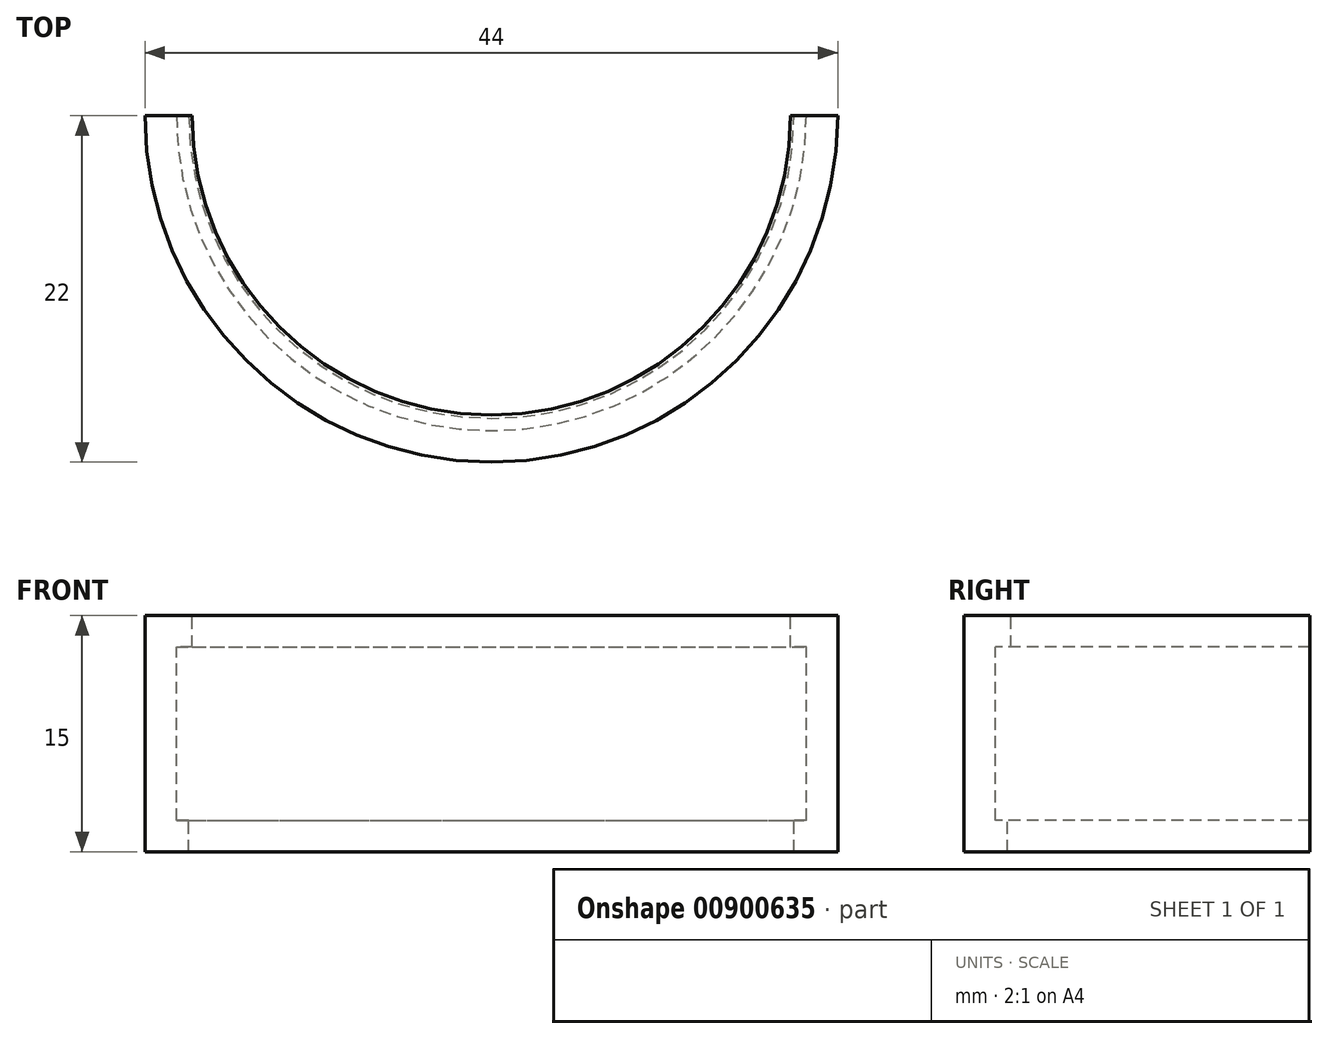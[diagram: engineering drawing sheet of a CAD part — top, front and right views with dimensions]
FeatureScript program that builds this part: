
annotation { "Feature Type Name" : "Feature", "Feature Type Description" : "" }
export const myFeature = defineFeature(function(context is Context, id is Id, definition is map)
    precondition{}
    {
        {
            var Q0;
            Q0=qCreatedBy(makeId("Front.planeOp"),FACE);
            var sketch = newSketch(context, id + "F0", { "sketchPlane" : qUnion([Q0])});
            skLineSegment(sketch, "E0.bottom", {"start": v(6.58, 13.02) * mm, "end": v(8.58, 13.02) * mm});
            skLineSegment(sketch, "E0.top", {"start": v(6.58, -1.98) * mm, "end": v(8.58, -1.98) * mm});
            skLineSegment(sketch, "E0.left", {"start": v(6.58, 11.02) * mm, "end": v(6.58, 0.02) * mm});
            skLineSegment(sketch, "E0.right", {"start": v(8.58, 13.02) * mm, "end": v(8.58, -1.98) * mm});
            skLineSegment(sketch, "E1.bottom", {"start": v(6.58, 13.02) * mm, "end": v(5.58, 13.02) * mm});
            skLineSegment(sketch, "E1.top", {"start": v(6.58, 11.02) * mm, "end": v(5.58, 11.02) * mm});
            skLineSegment(sketch, "E1.right", {"start": v(5.58, 13.02) * mm, "end": v(5.58, 11.02) * mm});
            skLineSegment(sketch, "E2.bottom", {"start": v(6.58, -1.98) * mm, "end": v(5.8, -1.98) * mm});
            skLineSegment(sketch, "E2.top", {"start": v(6.58, 0.02) * mm, "end": v(5.8, 0.02) * mm});
            skLineSegment(sketch, "E2.right", {"start": v(5.8, -1.98) * mm, "end": v(5.8, 0.02) * mm});
            skLineSegment(sketch, "E3", {"start": v(-13.42, 15.13) * mm, "end": v(-13.42, -5.88) * mm, "construction": true});
            skSolve(sketch);
        }
        {
            var Q0;
            Q0=makeQuery(id+"F0.imprint","IMPRINT",FACE,{"disambiguationData":[TD([[makeQuery(id+"F0.imprint","IMPRINT",EDGE,{"derivedFrom":sQuery(id+"F0.wireOp",EDGE,"E0.bottom")}),-1.0]])]});
            var Q1;
            Q1=sQuery(id+"F0.wireOp",EDGE,"E3");
            revolve(context, id + "F1", {"surfaceOperationType" : NewSurfaceOperationType.NEW, "entities" : qUnion([Q0]), "axis" : qUnion([Q1]), "revolveType" : RevolveType.FULL});
        }
        {
            var Q0;
            Q0=qCreatedBy(makeId("Front.planeOp"),FACE);
            var sketch = newSketch(context, id + "F2", { "sketchPlane" : qUnion([Q0])});
            skLineSegment(sketch, "E4.bottom", {"start": v(-52.77, 32.19) * mm, "end": v(31.61, 32.19) * mm});
            skLineSegment(sketch, "E4.top", {"start": v(-52.77, -29.43) * mm, "end": v(31.61, -29.43) * mm});
            skLineSegment(sketch, "E4.left", {"start": v(-52.77, 32.19) * mm, "end": v(-52.77, -29.43) * mm});
            skLineSegment(sketch, "E4.right", {"start": v(31.61, 32.19) * mm, "end": v(31.61, -29.43) * mm});
            skSolve(sketch);
        }
        {
            var Q0;
            Q0=makeQuery(id+"F2.imprint","IMPRINT",FACE,{"disambiguationData":[TD([[makeQuery(id+"F2.imprint","IMPRINT",EDGE,{"derivedFrom":sQuery(id+"F2.wireOp",EDGE,"E4.bottom")}),-1.0]])]});
            extrude(context, id + "F3", {"entities" : qUnion([Q0]), "operationType" : NewBodyOperationType.REMOVE, "oppositeDirection" : true, "depth" : 25 * mm, "offsetDistance" : 25 * mm});
        }
    });
